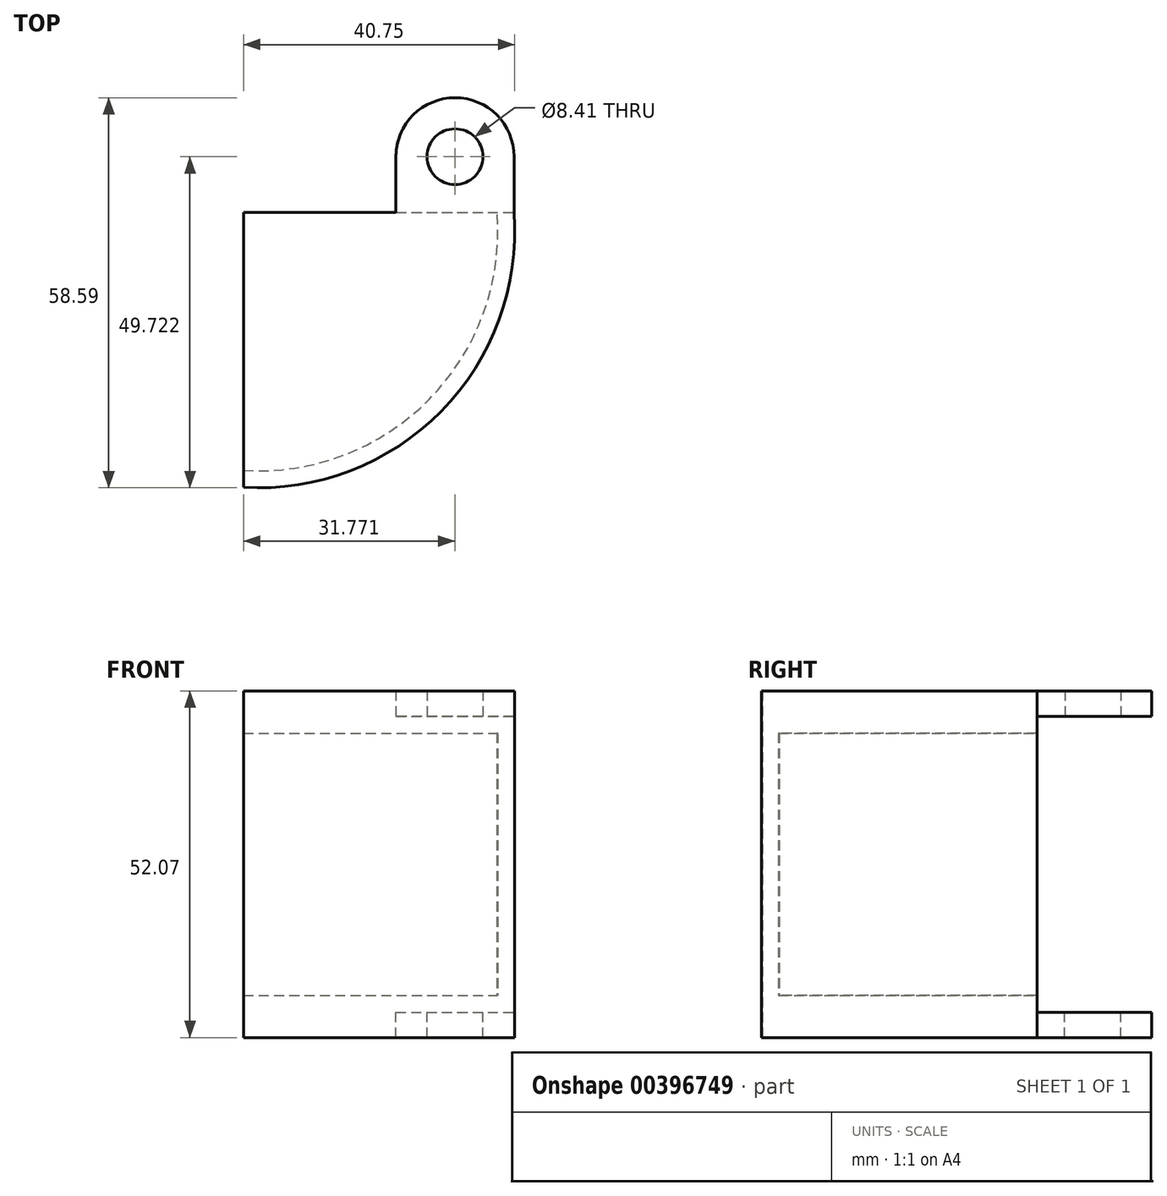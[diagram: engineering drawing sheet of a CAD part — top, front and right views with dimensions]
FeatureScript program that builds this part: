
annotation { "Feature Type Name" : "Feature", "Feature Type Description" : "" }
export const myFeature = defineFeature(function(context is Context, id is Id, definition is map)
    precondition{}
    {
        {
            var Q0;
            Q0=qCreatedBy(makeId("Top.planeOp"),FACE);
            var sketch = newSketch(context, id + "F0", { "sketchPlane" : qUnion([Q0])});
            skLineSegment(sketch, "E0", {"start": v(0, 0) * mm, "end": v(40.64, 0) * mm});
            skLineSegment(sketch, "E1", {"start": v(0, 0) * mm, "end": v(0, -41.28) * mm});
            skArc(sketch, "E2", {"start": v(0, -41.28) * mm, "mid": v(29.69, -29.86) * mm, "end": v(40.64, 0) * mm});
            skSolve(sketch);
        }
        {
            var Q0;
            Q0=makeQuery(id+"F0.imprint","IMPRINT",FACE,{"disambiguationData":[TD([[makeQuery(id+"F0.imprint","IMPRINT",EDGE,{"derivedFrom":sQuery(id+"F0.wireOp",EDGE,"E0")}),-1.0]])]});
            extrude(context, id + "F1", {"entities" : qUnion([Q0]), "depth" : 44.45 * mm});
        }
        {
            var Q0;
            Q0=makeQuery(id+"F1.opExtrude","SWEPT_FACE",FACE,{"disambiguationData":[OSD([sQuery(id+"F0.wireOp",EDGE,"E1")])]});
            var Q1;
            Q1=makeQuery(id+"F1.opExtrude","SWEPT_FACE",FACE,{"disambiguationData":[OSD([sQuery(id+"F0.wireOp",EDGE,"E0")])]});
            shell(context, id + "F2", {"entities" : qUnion([Q0, Q1]), "thickness" : 2.54 * mm});
        }
        {
            var Q0;
            Q0=makeQuery(id+"F1.opExtrude","CAP_FACE",FACE,{"disambiguationData":[OSD([sQuery(id+"F0.wireOp",EDGE,"E0"),sQuery(id+"F0.wireOp",EDGE,"E1"),sQuery(id+"F0.wireOp",EDGE,"E2")])],"isStart":false});
            var sketch = newSketch(context, id + "F3", { "sketchPlane" : qUnion([Q0])});
            skLineSegment(sketch, "E3", {"start": v(40.64, 0) * mm, "end": v(31.78, 0) * mm});
            skLineSegment(sketch, "E4", {"start": v(40.64, 0) * mm, "end": v(40.64, 8.4) * mm});
            skArc(sketch, "E5", {"start": v(40.64, 8.4) * mm, "mid": v(31.78, 17.25) * mm, "end": v(22.92, 8.4) * mm});
            skCircle(sketch, "E6", {"center": v(31.78, 8.4) * mm, "radius": 4.19 * mm});
            skLineSegment(sketch, "E7", {"start": v(31.78, 0) * mm, "end": v(22.92, 0) * mm});
            skLineSegment(sketch, "E8", {"start": v(22.92, 0) * mm, "end": v(22.92, 8.4) * mm});
            skLineSegment(sketch, "E9", {"start": v(31.78, 8.4) * mm, "end": v(31.78, 0) * mm});
            skSolve(sketch);
        }
        {
            var Q0;
            Q0=makeQuery(id+"F3.imprint","IMPRINT",FACE,{"disambiguationData":[TD([[makeQuery(id+"F3.imprint","IMPRINT",EDGE,{"derivedFrom":sQuery(id+"F3.wireOp",EDGE,"E3")}),1.0]])]});
            var Q1;
            Q1=makeQuery(id+"F3.imprint","IMPRINT",FACE,{"disambiguationData":[TD([[makeQuery(id+"F3.imprint","IMPRINT",EDGE,{"derivedFrom":sQuery(id+"F3.wireOp",EDGE,"E3")}),-1.0]])]});
            extrude(context, id + "F4", {"entities" : qUnion([Q0, Q1]), "operationType" : NewBodyOperationType.ADD, "depth" : 3.8 * mm});
        }
        {
            var Q0;
            Q0=makeQuery(id+"F1.opExtrude","CAP_FACE",FACE,{"disambiguationData":[OSD([sQuery(id+"F0.wireOp",EDGE,"E0"),sQuery(id+"F0.wireOp",EDGE,"E1"),sQuery(id+"F0.wireOp",EDGE,"E2")])],"isStart":true});
            var sketch = newSketch(context, id + "F5", { "sketchPlane" : qUnion([Q0])});
            skLineSegment(sketch, "E10", {"start": v(40.64, 0) * mm, "end": v(31.77, 0) * mm});
            skLineSegment(sketch, "E11", {"start": v(31.77, 0) * mm, "end": v(22.92, 0) * mm});
            skLineSegment(sketch, "E12", {"start": v(22.92, -8.38) * mm, "end": v(22.92, 0) * mm});
            skArc(sketch, "E13", {"start": v(22.92, -8.38) * mm, "mid": v(31.76, -17.24) * mm, "end": v(40.63, -8.4) * mm});
            skCircle(sketch, "E14", {"center": v(31.77, -8.38) * mm, "radius": 4.2 * mm});
            skLineSegment(sketch, "E15", {"start": v(40.64, 0) * mm, "end": v(40.63, -8.4) * mm});
            skSolve(sketch);
        }
        {
            var Q0;
            Q0=makeQuery(id+"F5.imprint","IMPRINT",FACE,{"disambiguationData":[TD([[makeQuery(id+"F5.imprint","IMPRINT",EDGE,{"derivedFrom":sQuery(id+"F5.wireOp",EDGE,"E10")}),1.0]])]});
            var Q1;
            Q1=makeQuery(id+"F5.imprint","IMPRINT",FACE,{"disambiguationData":[TD([[makeQuery(id+"F5.imprint","IMPRINT",EDGE,{"derivedFrom":sQuery(id+"F5.wireOp",EDGE,"E10")}),-1.0]])]});
            extrude(context, id + "F6", {"entities" : qUnion([Q0, Q1]), "operationType" : NewBodyOperationType.ADD, "depth" : 3.8 * mm});
        }
    });
